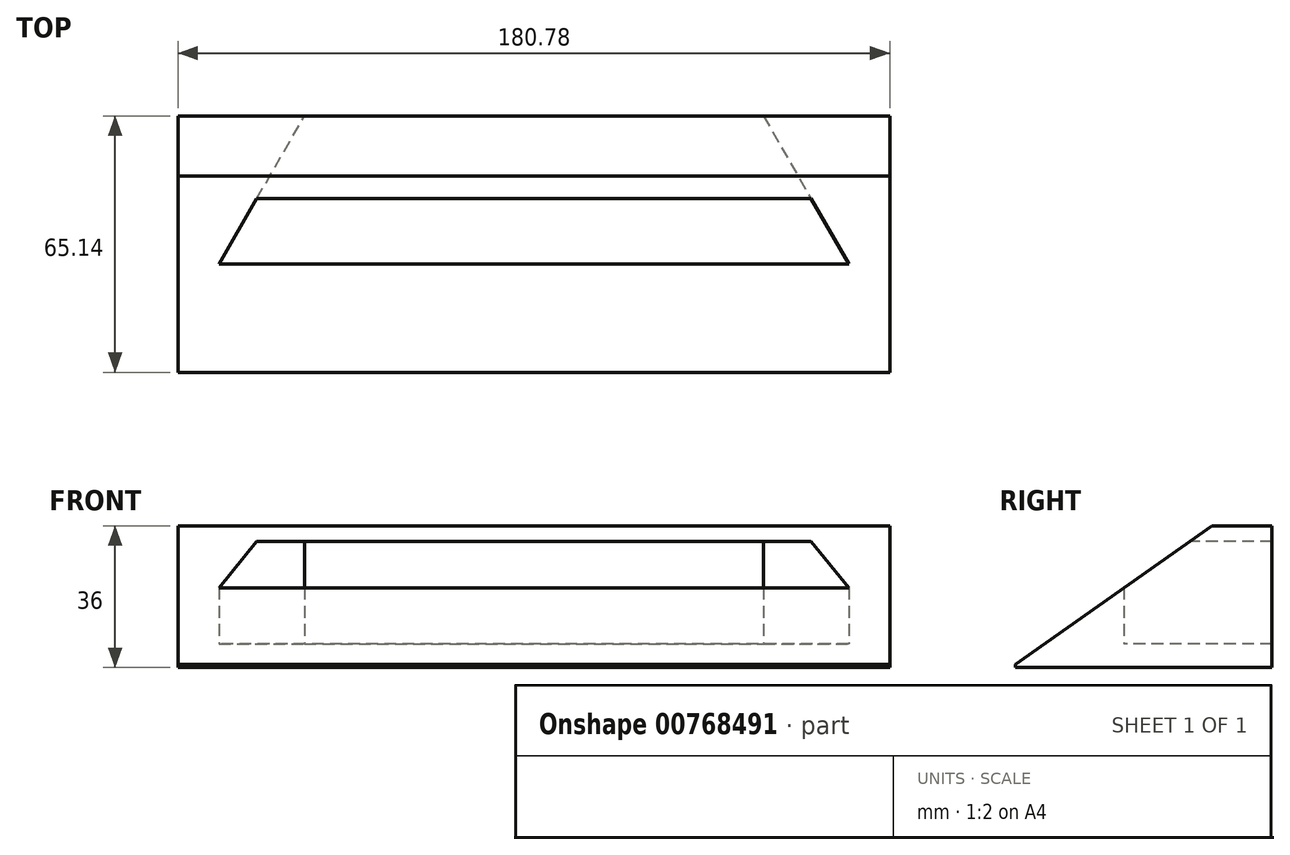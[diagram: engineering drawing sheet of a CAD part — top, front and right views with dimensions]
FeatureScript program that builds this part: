
annotation { "Feature Type Name" : "Feature", "Feature Type Description" : "" }
export const myFeature = defineFeature(function(context is Context, id is Id, definition is map)
    precondition{}
    {
        {
            var Q0;
            Q0=qCreatedBy(makeId("Top.planeOp"),FACE);
            var sketch = newSketch(context, id + "F0", { "sketchPlane" : qUnion([Q0])});
            skLineSegment(sketch, "E0.0", {"start": v(-80, -24) * mm, "end": v(0, 114.56) * mm});
            skLineSegment(sketch, "E0.1", {"start": v(0, 114.56) * mm, "end": v(80, -24) * mm});
            skLineSegment(sketch, "E0.2", {"start": v(80, -24) * mm, "end": v(-80, -24) * mm});
            skPoint(sketch, "E0.0.midPoint", {"position": v(-40, 45.28) * mm});
            skLineSegment(sketch, "E1", {"start": v(0, 126.56) * mm, "end": v(-90.4, -30) * mm});
            skLineSegment(sketch, "E2", {"start": v(-90.4, -30) * mm, "end": v(90.4, -30) * mm});
            skLineSegment(sketch, "E3", {"start": v(90.4, -30) * mm, "end": v(0, 126.56) * mm});
            skLineSegment(sketch, "E4", {"start": v(-90.4, -30) * mm, "end": v(-90.4, 0) * mm});
            skLineSegment(sketch, "E5", {"start": v(73.07, 0) * mm, "end": v(90.4, 0) * mm});
            skLineSegment(sketch, "E6", {"start": v(90.4, -30) * mm, "end": v(90.4, 0) * mm});
            skLineSegment(sketch, "E7", {"start": v(-90.4, 0) * mm, "end": v(-73.07, 0) * mm});
            skLineSegment(sketch, "E8", {"start": v(-58.29, 13.6) * mm, "end": v(58.29, 13.6) * mm});
            skLineSegment(sketch, "E9", {"start": v(-58.29, 13.6) * mm, "end": v(-65.21, 13.6) * mm});
            skLineSegment(sketch, "E10", {"start": v(58.29, 13.6) * mm, "end": v(65.21, 13.6) * mm});
            skLineSegment(sketch, "E11", {"start": v(-90.4, 0) * mm, "end": v(-90.4, 13.6) * mm});
            skLineSegment(sketch, "E12", {"start": v(-65.21, 13.6) * mm, "end": v(-90.4, 13.6) * mm});
            skLineSegment(sketch, "E13", {"start": v(90.4, 0) * mm, "end": v(90.4, 13.6) * mm});
            skLineSegment(sketch, "E14", {"start": v(65.21, 13.6) * mm, "end": v(90.4, 13.6) * mm});
            skLineSegment(sketch, "E15", {"start": v(-90.4, -30) * mm, "end": v(-90.4, -51.53) * mm});
            skLineSegment(sketch, "E16", {"start": v(-90.4, -51.53) * mm, "end": v(90.4, -51.53) * mm});
            skLineSegment(sketch, "E17", {"start": v(90.4, -30) * mm, "end": v(90.4, -51.53) * mm});
            skSolve(sketch);
        }
        {
            var Q0;
            {var subQ4=sQuery(id+"F0.wireOp",EDGE,"E0.2");Q0=makeQuery(id+"F0.imprint","IMPRINT",FACE,{"disambiguationData":[TD([[makeQuery(id+"F0.imprint","IMPRINT",EDGE,{"derivedFrom":subQ4}),1.0]])]});}
            var Q1;
            {var subQ0=sQuery(id+"F0.wireOp",EDGE,"E4");Q1=makeQuery(id+"F0.imprint","IMPRINT",FACE,{"disambiguationData":[TD([[makeQuery(id+"F0.imprint","IMPRINT",EDGE,{"derivedFrom":subQ0}),-1.0]])]});}
            var Q2;
            {var subQ0=sQuery(id+"F0.wireOp",EDGE,"E6");Q2=makeQuery(id+"F0.imprint","IMPRINT",FACE,{"disambiguationData":[TD([[makeQuery(id+"F0.imprint","IMPRINT",EDGE,{"derivedFrom":subQ0}),1.0]])]});}
            var Q3;
            {var subQ0=sQuery(id+"F0.wireOp",EDGE,"E7");Q3=makeQuery(id+"F0.imprint","IMPRINT",FACE,{"disambiguationData":[TD([[makeQuery(id+"F0.imprint","IMPRINT",EDGE,{"derivedFrom":subQ0}),1.0]])]});}
            var Q4;
            {var subQ0=sQuery(id+"F0.wireOp",EDGE,"E5");Q4=makeQuery(id+"F0.imprint","IMPRINT",FACE,{"disambiguationData":[TD([[makeQuery(id+"F0.imprint","IMPRINT",EDGE,{"derivedFrom":subQ0}),1.0]])]});}
            extrude(context, id + "F1", {"entities" : qUnion([Q0, Q1, Q2, Q3, Q4]), "depth" : 30 * mm, "offsetDistance" : 25 * mm});
        }
        {
            var Q0;
            Q0=makeQuery(id+"F1.opExtrude","CAP_EDGE",EDGE,{"disambiguationData":[OSD([sQuery(id+"F0.wireOp",EDGE,"E2")])],"isStart":false});
            chamfer(context, id + "F2", {"entities" : qUnion([Q0]), "chamferType" : ChamferType.OFFSET_ANGLE, "width" : 20 * mm, "oppositeDirection" : true, "angle" : 54.74 * degree, "tangentPropagation" : true});
        }
        {
            var Q0;
            {var subQ0=sQuery(id+"F0.wireOp",EDGE,"E0.2");Q0=makeQuery(id+"F0.imprint","IMPRINT",FACE,{"disambiguationData":[TD([[makeQuery(id+"F0.imprint","IMPRINT",EDGE,{"derivedFrom":subQ0}),-1.0]])]});}
            extrude(context, id + "F3", {"entities" : qUnion([Q0]), "operationType" : NewBodyOperationType.ADD, "depth" : 30 * mm, "offsetDistance" : 25 * mm});
        }
        {
            var Q0;
            Q0=makeQuery(id+"F2.opChamfer","BLEND_FACE",FACE,{"disambiguationData":[OSD([sQuery(id+"F0.wireOp",EDGE,"E2")])]});
            cPlane(context, id + "F4", {"entities" : qUnion([Q0]), "cplaneType" : CPlaneType.OFFSET, "offset" : 0 * mm, "width" : 150 * mm, "height" : 150 * mm});
        }
        {
            var Q0;
            Q0=qCreatedBy(id+"F4.planeOp",FACE);
            var sketch = newSketch(context, id + "F5", { "sketchPlane" : qUnion([Q0])});
            skLineSegment(sketch, "E18.bottom", {"start": v(-123.92, 59.92) * mm, "end": v(135.6, 59.92) * mm});
            skLineSegment(sketch, "E18.top", {"start": v(-123.92, -61.5) * mm, "end": v(135.6, -61.5) * mm});
            skLineSegment(sketch, "E18.left", {"start": v(-123.92, 59.92) * mm, "end": v(-123.92, -61.5) * mm});
            skLineSegment(sketch, "E18.right", {"start": v(135.6, 59.92) * mm, "end": v(135.6, -61.5) * mm});
            skSolve(sketch);
        }
        {
            var Q0;
            Q0=makeQuery(id+"F0.imprint","IMPRINT",FACE,{"disambiguationData":[TD([[makeQuery(id+"F0.imprint","IMPRINT",EDGE,{"derivedFrom":sQuery(id+"F0.wireOp",EDGE,"E2")}),-1.0]])]});
            extrude(context, id + "F6", {"entities" : qUnion([Q0]), "operationType" : NewBodyOperationType.ADD, "depth" : 25 * mm, "offsetDistance" : 25 * mm});
        }
        {
            var Q0;
            {var subQ0=sQuery(id+"F0.wireOp",EDGE,"E0.2");Q0=makeQuery(id+"F0.imprint","IMPRINT",FACE,{"disambiguationData":[TD([[makeQuery(id+"F0.imprint","IMPRINT",EDGE,{"derivedFrom":subQ0}),-1.0]])]});}
            var Q1;
            {var subQ3=sQuery(id+"F0.wireOp",EDGE,"E0.2");Q1=makeQuery(id+"F0.imprint","IMPRINT",FACE,{"disambiguationData":[TD([[makeQuery(id+"F0.imprint","IMPRINT",EDGE,{"derivedFrom":subQ3}),1.0]])]});}
            var Q2;
            {var subQ0=sQuery(id+"F0.wireOp",EDGE,"E4");Q2=makeQuery(id+"F0.imprint","IMPRINT",FACE,{"disambiguationData":[TD([[makeQuery(id+"F0.imprint","IMPRINT",EDGE,{"derivedFrom":subQ0}),-1.0]])]});}
            var Q3;
            {var subQ0=sQuery(id+"F0.wireOp",EDGE,"E7");Q3=makeQuery(id+"F0.imprint","IMPRINT",FACE,{"disambiguationData":[TD([[makeQuery(id+"F0.imprint","IMPRINT",EDGE,{"derivedFrom":subQ0}),1.0]])]});}
            var Q4;
            {var subQ0=sQuery(id+"F0.wireOp",EDGE,"E5");Q4=makeQuery(id+"F0.imprint","IMPRINT",FACE,{"disambiguationData":[TD([[makeQuery(id+"F0.imprint","IMPRINT",EDGE,{"derivedFrom":subQ0}),1.0]])]});}
            var Q5;
            {var subQ2=sQuery(id+"F0.wireOp",EDGE,"E5");Q5=makeQuery(id+"F0.imprint","IMPRINT",FACE,{"disambiguationData":[TD([[makeQuery(id+"F0.imprint","IMPRINT",EDGE,{"derivedFrom":subQ2}),-1.0]])]});}
            var Q6;
            Q6=makeQuery(id+"F0.imprint","IMPRINT",FACE,{"disambiguationData":[TD([[makeQuery(id+"F0.imprint","IMPRINT",EDGE,{"derivedFrom":sQuery(id+"F0.wireOp",EDGE,"E2")}),-1.0]])]});
            extrude(context, id + "F7", {"entities" : qUnion([Q0, Q1, Q2, Q3, Q4, Q5, Q6]), "operationType" : NewBodyOperationType.ADD, "oppositeDirection" : true, "depth" : 6 * mm, "offsetDistance" : 25 * mm});
        }
        {
            var Q0;
            Q0=makeQuery(id+"F5.imprint","IMPRINT",FACE,{"disambiguationData":[TD([[makeQuery(id+"F5.imprint","IMPRINT",EDGE,{"derivedFrom":sQuery(id+"F5.wireOp",EDGE,"E18.bottom")}),-1.0]])]});
            extrude(context, id + "F8", {"entities" : qUnion([Q0]), "operationType" : NewBodyOperationType.REMOVE, "depth" : 25 * mm, "offsetDistance" : 25 * mm});
        }
        {
            var Q0;
            {var subQ0=sQuery(id+"F0.wireOp",EDGE,"E0.2");Q0=makeQuery(id+"F0.imprint","IMPRINT",FACE,{"disambiguationData":[TD([[makeQuery(id+"F0.imprint","IMPRINT",EDGE,{"derivedFrom":subQ0}),-1.0]])]});}
            extrude(context, id + "F9", {"entities" : qUnion([Q0]), "operationType" : NewBodyOperationType.REMOVE, "depth" : 26 * mm, "offsetDistance" : 25 * mm});
        }
        {
            var Q0;
            Q0=makeQuery(id+"F9.boolean.opBoolean","COPY",FACE,{"derivedFrom":makeQuery(id+"F9.opExtrude","SWEPT_FACE",FACE,{"disambiguationData":[OSD([sQuery(id+"F0.wireOp",EDGE,"E0.2")])]})});
            cPlane(context, id + "F10", {"entities" : qUnion([Q0]), "cplaneType" : CPlaneType.OFFSET, "offset" : 0 * mm, "width" : 150 * mm, "height" : 150 * mm});
        }
    });
